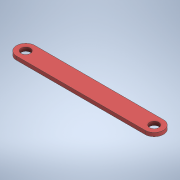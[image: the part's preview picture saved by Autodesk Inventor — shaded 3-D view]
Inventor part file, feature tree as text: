
AUTODESK INVENTOR PART (.ipt)
format: ipt  version: 2020.1 (Build 241239000, 239)  size: 118,784 bytes
history: native  units: in
note: dims shown in document units (in); Inventor stores cm internally (conversion verified against a paired STEP export)
features: extrude x1, sketch x1
ambient origin geometry x8: Origin, YZ Plane, XZ Plane, XY Plane, X Axis, Y Axis, Z Axis, Center Point
bodies: Solid1 (feature_tree)
feature tree (2):
  extrude  "Extrusion1"  Depth=10.0in
  sketch  "Sketch1"  dims[d0=70.0in d1=10.0in d2=5.0in d3=5.0in d4=2.0in d5=0.0in]
